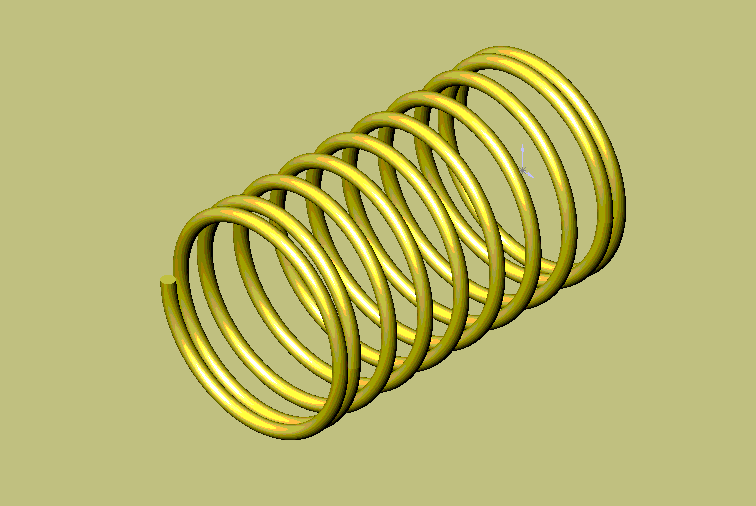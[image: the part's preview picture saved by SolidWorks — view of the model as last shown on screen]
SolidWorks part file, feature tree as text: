
SOLIDWORKS PART (.sldprt)
format: sldprt  version: not decoded by parser v0  size: 2,978,304 bytes
history: native  units: mm
features: sketch x6, plane x4, sweep x3, material x1, helix x1 (+8 scaffold rows collapsed)
feature tree (23):
  scaffold x8  (default folders/planes/origin — collapsed)
  material  "Matériau <non spécifié>"
  plane  "Plane1"
  plane  "Plane2"
  plane  "Plane3"
  sketch  "Esquisse1"  dims[D1=14.5mm]
  helix  "Hélice1"  Pitch=22.05mm
  sketch  "Esquisse2"  dims[D1=1.0mm]
  sweep  "Base-Balayage"
  sketch  "Esquisse3"  dims[D1=14.5mm Hélice2=0.0 D3=1.65mm D4=1.1mm D5=1500.0mm]
  sketch  "Esquisse5"
  sweep  "Boss.-Balayage5"
  sketch  "Esquisse7"  dims[D1=~0.559017mm]
  plane  "Plan1"
  sketch  "Esquisse8"  dims[Hélice3=0.0 D3=1.65mm D4=1.1mm D5=1500.0mm]
  sweep  "Boss.-Balayage6"
decode coverage: 6 of 10 modeling features carry decoded parameters
note: ~ marks probable driven/reference dimensions
note: suppression state not decoded; provenance and decode notes live in map.json
